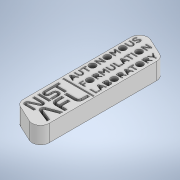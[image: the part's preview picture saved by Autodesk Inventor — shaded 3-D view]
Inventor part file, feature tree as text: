
AUTODESK INVENTOR PART (.ipt)
format: ipt  version: 2020 (Build 240168000, 168)  size: 954,880 bytes
history: native  units: in
note: dims shown in document units (in); Inventor stores cm internally (conversion verified against a paired STEP export)
features: extrude x1, fillet x1, sketch x1
ambient origin geometry x8: Origin, YZ Plane, XZ Plane, XY Plane, X Axis, Y Axis, Z Axis, Center Point
bodies: Solid1 (feature_tree)
feature tree (3):
  extrude  "Extrusion1"  Depth=0.5in
  fillet  "Fillet1"  Radius=0.7902in
  sketch  "Sketch1"  dims[d0=0.86in d8=7.5in d9=0.7902in d10=0.1718in d11=1.0in d12=0.0in d13=0.5in d14=0.5in d15=0.0344in d16=0.5in d17=0.0344in]
